# Revit family: RRHDWSRRING
name_source: partatom
category: Generic Models
revit_build: Autodesk Revit 2018 (Build: 20190510_1515(x64)
units: mm (PartAtom-declared; Revit-internal decimal feet)

## family parameters
Always vertical = No
Can host rebar = No
Cut with Voids When Loaded = No
Part Type = Normal
Room Calculation Point = No
Round Connector Dimension = Use Diameter
Shared = No
Work Plane-Based = Yes

## types (4) — shared parameters
Default Elevation = 48 "
Ring Material = <By Category>

## per-type parameters (varying)
| type | 114 Tail | 114in | 2 Tail | 2in | Description | Tail |
| RRHDWSRRING11/4 | Yes | Yes | No | No | Cable Management Rocket Ring™ 304 1/4 Inch X 1 1/4 Inch | Yes |
| RRHDWSRRING2 | No | No | Yes | Yes | Cable Management Rocket Ring™ 304 1/4 Inch X 2 Inch | Yes |
| RRHDWSRRING11/4NT | No | Yes | No | No | Cable Management Rocket Ring™ 304 1/4 Inch X 1 1/4 Inch No Tail | No |
| RRHDWSRRING2NT | No | No | No | Yes | Cable Management Rocket Ring™ 304 1/4 Inch X 2 Inch No Tail | No |

note: column(s) folded — value = type name in every type: Catalog Number

## geometry (parser evidence)
native form markers: Sweep x3
no freeform markers — native parametric forms only
